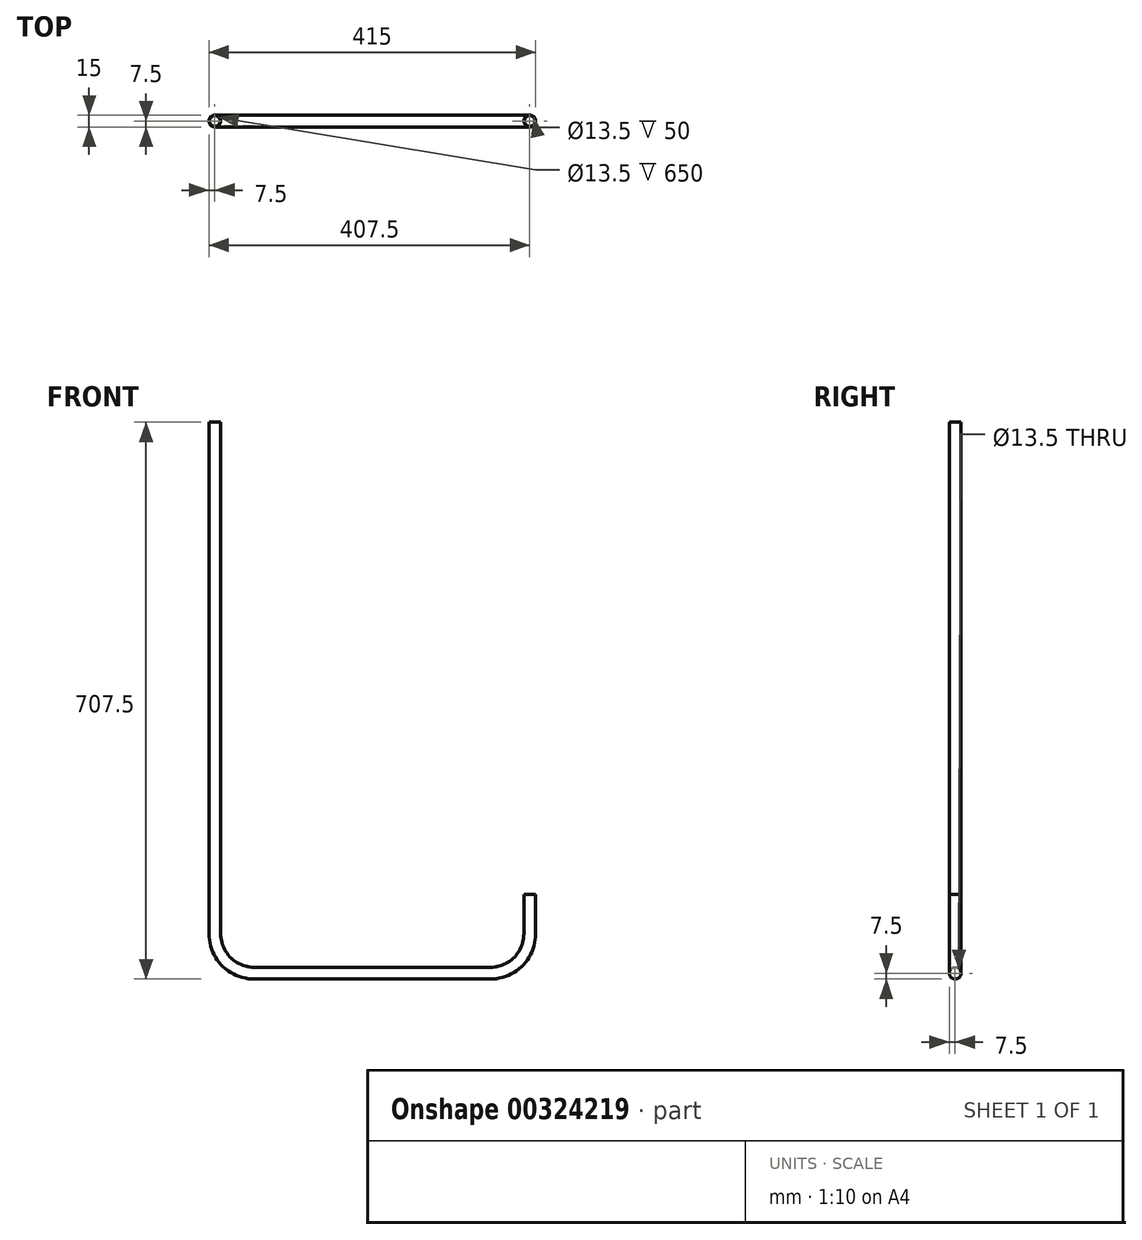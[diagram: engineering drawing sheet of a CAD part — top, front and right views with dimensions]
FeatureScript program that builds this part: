
annotation { "Feature Type Name" : "Feature", "Feature Type Description" : "" }
export const myFeature = defineFeature(function(context is Context, id is Id, definition is map)
    precondition{}
    {
        {
            var Q0;
            Q0=qCreatedBy(makeId("Front.planeOp"),FACE);
            var sketch = newSketch(context, id + "F0", { "sketchPlane" : qUnion([Q0])});
            skLineSegment(sketch, "E0", {"start": v(0, 0) * mm, "end": v(0, -650) * mm});
            skLineSegment(sketch, "E1", {"start": v(50, -700) * mm, "end": v(350, -700) * mm});
            skLineSegment(sketch, "E2", {"start": v(400, -650) * mm, "end": v(400, -600) * mm});
            skPoint(sketch, "E3.visualSharp", {"position": v(0, -700) * mm});
            skArc(sketch, "E3.filletArc", {"start": v(0, -650) * mm, "mid": v(14.64, -685.36) * mm, "end": v(50, -700) * mm});
            skPoint(sketch, "E4.visualSharp", {"position": v(400, -700) * mm});
            skArc(sketch, "E4.filletArc", {"start": v(350, -700) * mm, "mid": v(385.36, -685.36) * mm, "end": v(400, -650) * mm});
            skSolve(sketch);
        }
        {
            var Q0;
            Q0=qCreatedBy(makeId("Top.planeOp"),FACE);
            var sketch = newSketch(context, id + "F1", { "sketchPlane" : qUnion([Q0])});
            skCircle(sketch, "E5", {"center": v(0, 0) * mm, "radius": 7.5 * mm});
            skCircle(sketch, "E6", {"center": v(0, 0) * mm, "radius": 6.75 * mm});
            skSolve(sketch);
        }
        {
            var Q0;
            Q0=makeQuery(id+"F1.imprint","IMPRINT",FACE,{"disambiguationData":[TD([[makeQuery(id+"F1.imprint","IMPRINT",EDGE,{"derivedFrom":sQuery(id+"F1.wireOp",EDGE,"E5")}),1.0]])]});
            var Q1;
            Q1=sQuery(id+"F0.wireOp",EDGE,"E0");
            var Q2;
            Q2=sQuery(id+"F0.wireOp",EDGE,"E3.filletArc");
            var Q3;
            Q3=sQuery(id+"F0.wireOp",EDGE,"E1");
            var Q4;
            Q4=sQuery(id+"F0.wireOp",EDGE,"E4.filletArc");
            var Q5;
            Q5=sQuery(id+"F0.wireOp",EDGE,"E2");
            sweep(context, id + "F2", {"profiles" : qUnion([Q0]), "path" : qUnion([Q1, Q2, Q3, Q4, Q5])});
        }
    });
